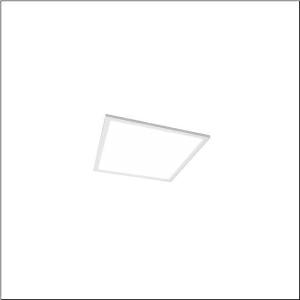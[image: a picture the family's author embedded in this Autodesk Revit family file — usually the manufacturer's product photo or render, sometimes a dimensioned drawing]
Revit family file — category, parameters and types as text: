
# Revit family: apollon_21_square_51mq13wd2414
name_source: partatom
category: Lighting Fixtures
units: mm (PartAtom-declared; Revit-internal decimal feet)

## family parameters
Cut with Voids When Loaded = No
Host = Face
Light Source = No
Part Type = Normal
Room Calculation Point = No
Round Connector Dimension = Use Diameter
Shared = No

## types (1)
- Apollon 21 square (1 x LED, 1800 lm, 14 W, 4000K)
    Apparent Load = 14 VA
    CIE Flux Codes = 68 89 97 100 100
    Color Rendering = 80
    Color Temperature = 4000K
    Default Elevation = 1800 mm  [stored 5.90551 ft]
    Description = Apollon 21 square, office luminaire, primary optical cover: micro prismatic cover, of PMMA, light emission: direct distribution, primary light characteristic: symmetric, installation type: recessed, LED, rated luminous flux: 1.800lm, luminous efficacy: 129lm/W, light colour: 840, colour temperature: 4000K, control gear: DALI 2, with terminal, 5-pole, mains connection: 220..240V, AC/DC, 0/50..60Hz, rated input power: 14W, suitable for self-contained emergency lighting element 59MQE002602A with integrated self-test function according to EN 60598-2-22, housing, of sheet steel, coated, traffic white (RAL 9016), with rapid mounting bracket, length: 296mm, width: 296mm, height: 55mm, housing upper side, of sheet steel, galvanised, protection rating (complete): IP20, protection rating (lamp compartment, on room side): IP50, insulation class (complete): insulation class II (safety insulation), certification: CE, ENEC, impact resistance: IK03, permissible operating ambient temperature: -20..+45°C, standard: EN 60598-2-22, corresponds to IFS (International Featured Standards) requirements for safety and quality in the food industry, packaging unit: 1 piece
    Height = 0 mm  [stored 0 ft]
    Lamp = 1 x LED
    Lamp Light Flux = 1800 lm
    Lamp Power = 14 W
    Lamp count = 1
    Length = 295 mm
    Luminous efficacy = 129 lm/W
    Manufacturer = Siteco
    ModVariant = No
    Model = 51MQ13WD2414
    Mounting Place = Ceiling
    Mounting Type = Recessed
    Number of Poles = 1
    OnlyDefault = Yes
    Power Factor = 1
    Product Name = Apollon 21 square
    Product group = office luminaire | ceiling recessed
    ProductGroupID = 400
    Protection Class = Protection class II
    Protection Degree = IP 20
    RLX_Detail_Level = 1
    RLX_Emergency_Light_Flux = 0 lm
    RLX_Emergency_Type = 0
    RLX_Emergency_Type_DB = No
    RlxData = <blob elided: 9577 chars, md5=3f87a13c>
    Socket = socket
    Standby Power = 0 W
    System Light Flux = 1800 lm
    System Power = 14 W
    Type Comments = Product without accessories
    Type Image = l_1291030.jpg
    URL = http://relux.com
    VarID = ---
    Voltage = 0 V
    Weight = 0.00 kg
    Width = 295 mm

note: [stored X ft] marks values corroborated as IEEE doubles in the binary element streams (Revit-internal decimal feet)

## geometry (parser evidence)
native form markers: Sweep x9
no freeform markers — native parametric forms only
